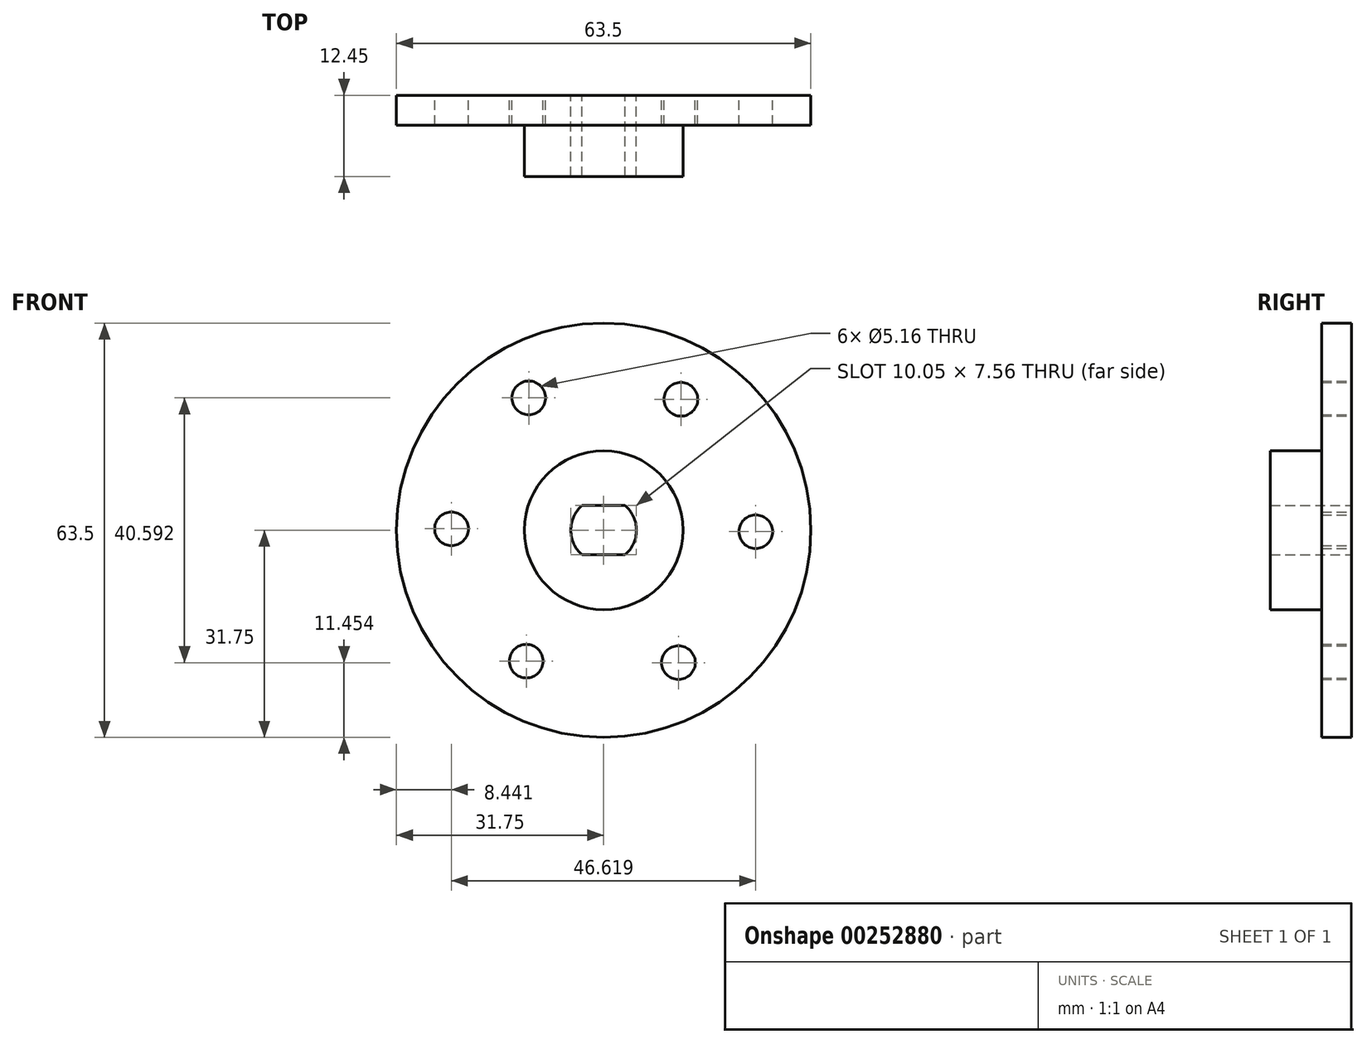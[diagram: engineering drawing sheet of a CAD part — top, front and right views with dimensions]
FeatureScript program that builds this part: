
annotation { "Feature Type Name" : "Feature", "Feature Type Description" : "" }
export const myFeature = defineFeature(function(context is Context, id is Id, definition is map)
    precondition{}
    {
        {
            var Q0;
            Q0=qCreatedBy(makeId("Front.planeOp"),FACE);
            var sketch = newSketch(context, id + "F0", { "sketchPlane" : qUnion([Q0])});
            skCircle(sketch, "E0", {"center": v(0, 0) * mm, "radius": 31.75 * mm});
            skArc(sketch, "E1", {"start": v(3.3, -3.78) * mm, "mid": v(5.02, 0) * mm, "end": v(3.3, 3.78) * mm});
            skArc(sketch, "E2", {"start": v(-3.3, 3.78) * mm, "mid": v(-5.02, 0) * mm, "end": v(-3.3, -3.78) * mm});
            skCircle(sketch, "E3", {"center": v(0, 0) * mm, "radius": 12.17 * mm});
            skCircle(sketch, "E4", {"center": v(11.84, 20.08) * mm, "radius": 2.58 * mm});
            skCircle(sketch, "E5", {"center": v(-11.47, 20.3) * mm, "radius": 2.58 * mm});
            skCircle(sketch, "E6", {"center": v(-23.3, 0.22) * mm, "radius": 2.58 * mm});
            skCircle(sketch, "E7", {"center": v(-11.84, -20.08) * mm, "radius": 2.58 * mm});
            skCircle(sketch, "E8", {"center": v(11.47, -20.3) * mm, "radius": 2.58 * mm});
            skCircle(sketch, "E9", {"center": v(23.3, -0.22) * mm, "radius": 2.58 * mm});
            skLineSegment(sketch, "E10.bottom", {"start": v(-3.3, -3.78) * mm, "end": v(3.3, -3.78) * mm});
            skLineSegment(sketch, "E10.top", {"start": v(-3.3, 3.78) * mm, "end": v(3.3, 3.78) * mm});
            skSolve(sketch);
        }
        {
            var Q0;
            Q0=makeQuery(id+"F0.imprint","IMPRINT",FACE,{"disambiguationData":[TD([[makeQuery(id+"F0.imprint","IMPRINT",EDGE,{"derivedFrom":sQuery(id+"F0.wireOp",EDGE,"E3")}),1.0]])]});
            extrude(context, id + "F1", {"entities" : qUnion([Q0]), "depth" : 12.45 * mm});
        }
        {
            var Q0;
            Q0=makeQuery(id+"F0.imprint","IMPRINT",FACE,{"disambiguationData":[TD([[makeQuery(id+"F0.imprint","IMPRINT",EDGE,{"derivedFrom":sQuery(id+"F0.wireOp",EDGE,"E0")}),1.0]])]});
            extrude(context, id + "F2", {"entities" : qUnion([Q0]), "operationType" : NewBodyOperationType.ADD, "depth" : 4.57 * mm});
        }
    });
